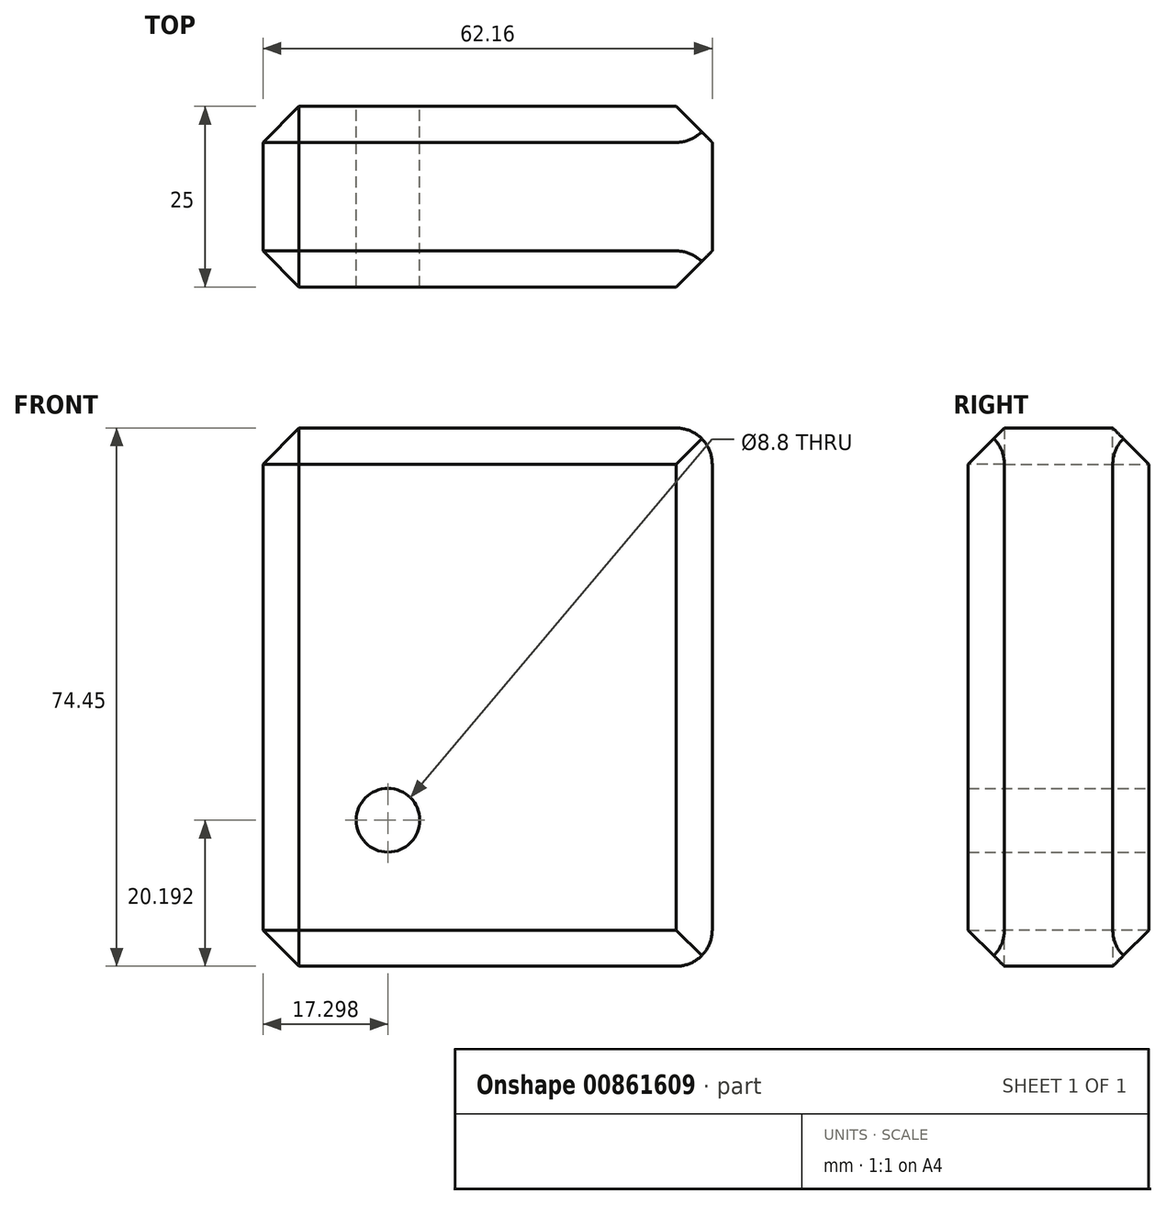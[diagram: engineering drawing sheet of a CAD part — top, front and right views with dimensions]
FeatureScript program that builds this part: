
annotation { "Feature Type Name" : "Feature", "Feature Type Description" : "" }
export const myFeature = defineFeature(function(context is Context, id is Id, definition is map)
    precondition{}
    {
        {
            var Q0;
            Q0=qCreatedBy(makeId("Front.planeOp"),FACE);
            var sketch = newSketch(context, id + "F0", { "sketchPlane" : qUnion([Q0])});
            skLineSegment(sketch, "E0.bottom", {"start": v(-27.94, 35.3) * mm, "end": v(34.22, 35.3) * mm});
            skLineSegment(sketch, "E0.top", {"start": v(-27.94, -39.15) * mm, "end": v(34.22, -39.15) * mm});
            skLineSegment(sketch, "E0.left", {"start": v(-27.94, 35.3) * mm, "end": v(-27.94, -39.15) * mm});
            skLineSegment(sketch, "E0.right", {"start": v(34.22, 35.3) * mm, "end": v(34.22, -39.15) * mm});
            skSolve(sketch);
        }
        {
            var Q0;
            Q0 = qSketchRegion(id + "F0", true);
            var Q1;
            Q1=makeQuery(id+"F0.imprint","IMPRINT",FACE,{"disambiguationData":[TD([[makeQuery(id+"F0.imprint","IMPRINT",EDGE,{"derivedFrom":sQuery(id+"F0.wireOp",EDGE,"E0.bottom")}),-1.0]])]});
            extrude(context, id + "F1", {"entities" : qUnion([Q0, Q1]), "depth" : 25 * mm, "offsetDistance" : 25 * mm});
        }
        {
            var Q0;
            Q0=makeQuery(id+"F1.opExtrude","CAP_EDGE",EDGE,{"disambiguationData":[OSD([sQuery(id+"F0.wireOp",EDGE,"E0.left")])],"isStart":true});
            var Q1;
            Q1=makeQuery(id+"F1.opExtrude","CAP_FACE",FACE,{"disambiguationData":[OSD([sQuery(id+"F0.wireOp",EDGE,"E0.bottom"),sQuery(id+"F0.wireOp",EDGE,"E0.top"),sQuery(id+"F0.wireOp",EDGE,"E0.left"),sQuery(id+"F0.wireOp",EDGE,"E0.right")])],"isStart":false});
            var Q2;
            Q2=makeQuery(id+"F1.opExtrude","SWEPT_FACE",FACE,{"disambiguationData":[OSD([sQuery(id+"F0.wireOp",EDGE,"E0.left")])]});
            var Q3;
            Q3=makeQuery(id+"F1.opExtrude","CAP_EDGE",EDGE,{"disambiguationData":[OSD([sQuery(id+"F0.wireOp",EDGE,"E0.top")])],"isStart":true});
            var Q4;
            Q4=makeQuery(id+"F1.opExtrude","CAP_EDGE",EDGE,{"disambiguationData":[OSD([sQuery(id+"F0.wireOp",EDGE,"E0.right")])],"isStart":true});
            var Q5;
            Q5=makeQuery(id+"F1.opExtrude","CAP_EDGE",EDGE,{"disambiguationData":[OSD([sQuery(id+"F0.wireOp",EDGE,"E0.bottom")])],"isStart":true});
            chamfer(context, id + "F2", {"entities" : qUnion([Q0, Q1, Q2, Q3, Q4, Q5]), "width" : 5 * mm, "tangentPropagation" : true});
        }
        {
            var Q0;
            Q0=makeQuery(id+"F1.opExtrude","CAP_FACE",FACE,{"disambiguationData":[OSD([sQuery(id+"F0.wireOp",EDGE,"E0.bottom"),sQuery(id+"F0.wireOp",EDGE,"E0.top"),sQuery(id+"F0.wireOp",EDGE,"E0.left"),sQuery(id+"F0.wireOp",EDGE,"E0.right")])],"isStart":true});
            var sketch = newSketch(context, id + "F3", { "sketchPlane" : qUnion([Q0])});
            skCircle(sketch, "E1", {"center": v(10.64, -18.96) * mm, "radius": 4.02 * mm});
            skSolve(sketch);
        }
        {
            var Q0;
            Q0=sQuery(id+"F3.wireOp",VERTEX,"E1.center");
            var Q1;
            Q1=makeQuery(id+"F1.opExtrude","SWEPT_BODY",BODY,{"disambiguationData":[OSD([sQuery(id+"F0.wireOp",EDGE,"E0.bottom"),sQuery(id+"F0.wireOp",EDGE,"E0.top"),sQuery(id+"F0.wireOp",EDGE,"E0.left"),sQuery(id+"F0.wireOp",EDGE,"E0.right")])]});
            hole(context, id + "F4", {"style" : HoleStyle.SIMPLE, "endStyle" : HoleEndStyle.THROUGH, "standardTappedOrClearance" : lookupTablePath({ "fit" : "Normal", "standard" : "ISO", "size" : "M8", "type" : "Clearance" }), "standardBlindInLast" : lookupTablePath({ "fit" : "Standard", "standard" : "ISO", "size" : "M8", "type" : "Clearance" }), "holeDiameter" : 8.8 * mm, "majorDiameter" : 8 * mm, "isTappedThrough" : true, "tappedDepth" : 12 * mm, "tapClearance" : 3, "startFromSketch" : true, "locations" : qUnion([Q0]), "scope" : qUnion([Q1])});
        }
        {
            var Q0;
            Q0=makeQuery(id+"F1.opExtrude","SWEPT_EDGE",EDGE,{"disambiguationData":[OSD([sQuery(id+"F0.wireOp",EDGE,"E0.top"),sQuery(id+"F0.wireOp",EDGE,"E0.right")])]});
            fillet(context, id + "F5", {"entities" : qUnion([Q0]), "radius" : 5 * mm, "tangentPropagation" : true, "allowEdgeOverflow" : false});
        }
        {
            var Q0;
            Q0=makeQuery(id+"F1.opExtrude","SWEPT_EDGE",EDGE,{"disambiguationData":[OSD([sQuery(id+"F0.wireOp",EDGE,"E0.bottom"),sQuery(id+"F0.wireOp",EDGE,"E0.right")])]});
            fillet(context, id + "F6", {"entities" : qUnion([Q0]), "radius" : 5 * mm, "tangentPropagation" : true, "allowEdgeOverflow" : false});
        }
    });
